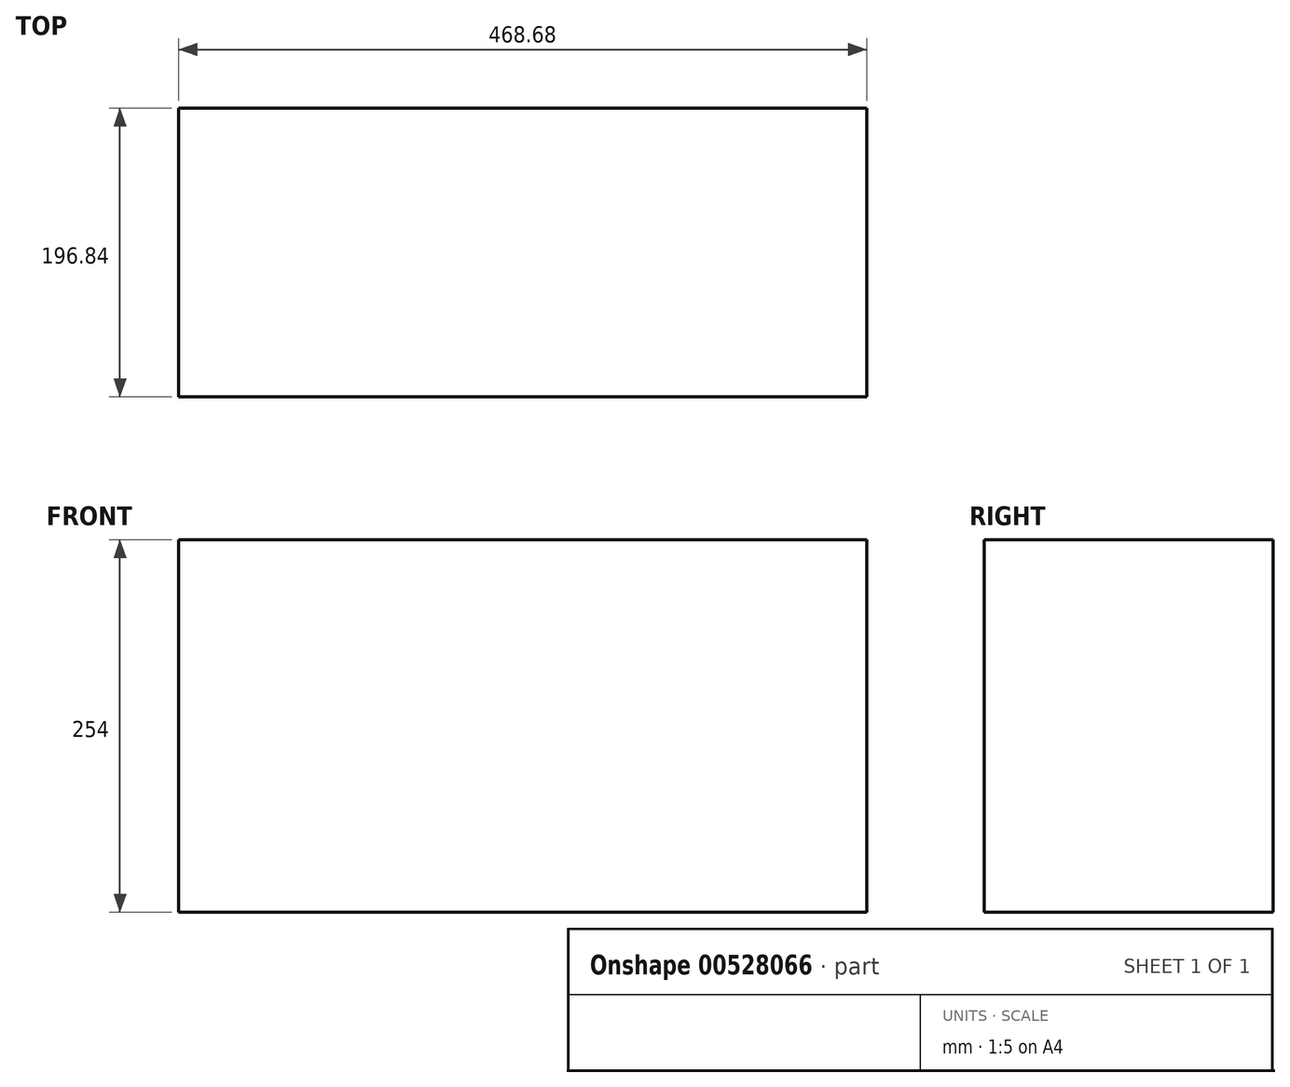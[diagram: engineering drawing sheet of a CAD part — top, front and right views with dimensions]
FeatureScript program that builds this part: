
annotation { "Feature Type Name" : "Feature", "Feature Type Description" : "" }
export const myFeature = defineFeature(function(context is Context, id is Id, definition is map)
    precondition{}
    {
        {
            var Q0;
            Q0=qCreatedBy(makeId("Top.planeOp"),FACE);
            var sketch = newSketch(context, id + "F0", { "sketchPlane" : qUnion([Q0])});
            skLineSegment(sketch, "E0.bottom", {"start": v(234.34, 98.43) * mm, "end": v(-234.34, 98.43) * mm});
            skLineSegment(sketch, "E0.top", {"start": v(234.34, -98.43) * mm, "end": v(-234.34, -98.43) * mm});
            skLineSegment(sketch, "E0.left", {"start": v(234.34, 98.43) * mm, "end": v(234.34, -98.43) * mm});
            skLineSegment(sketch, "E0.right", {"start": v(-234.34, 98.43) * mm, "end": v(-234.34, -98.43) * mm});
            skPoint(sketch, "E0.middle", {"position": v(0, 0) * mm});
            skSolve(sketch);
        }
        {
            var Q0;
            Q0 = qSketchRegion(id + "F0", true);
            extrude(context, id + "F1", {"entities" : qUnion([Q0]), "depth" : 254 * mm, "offsetDistance" : 25.4 * mm});
        }
    });
